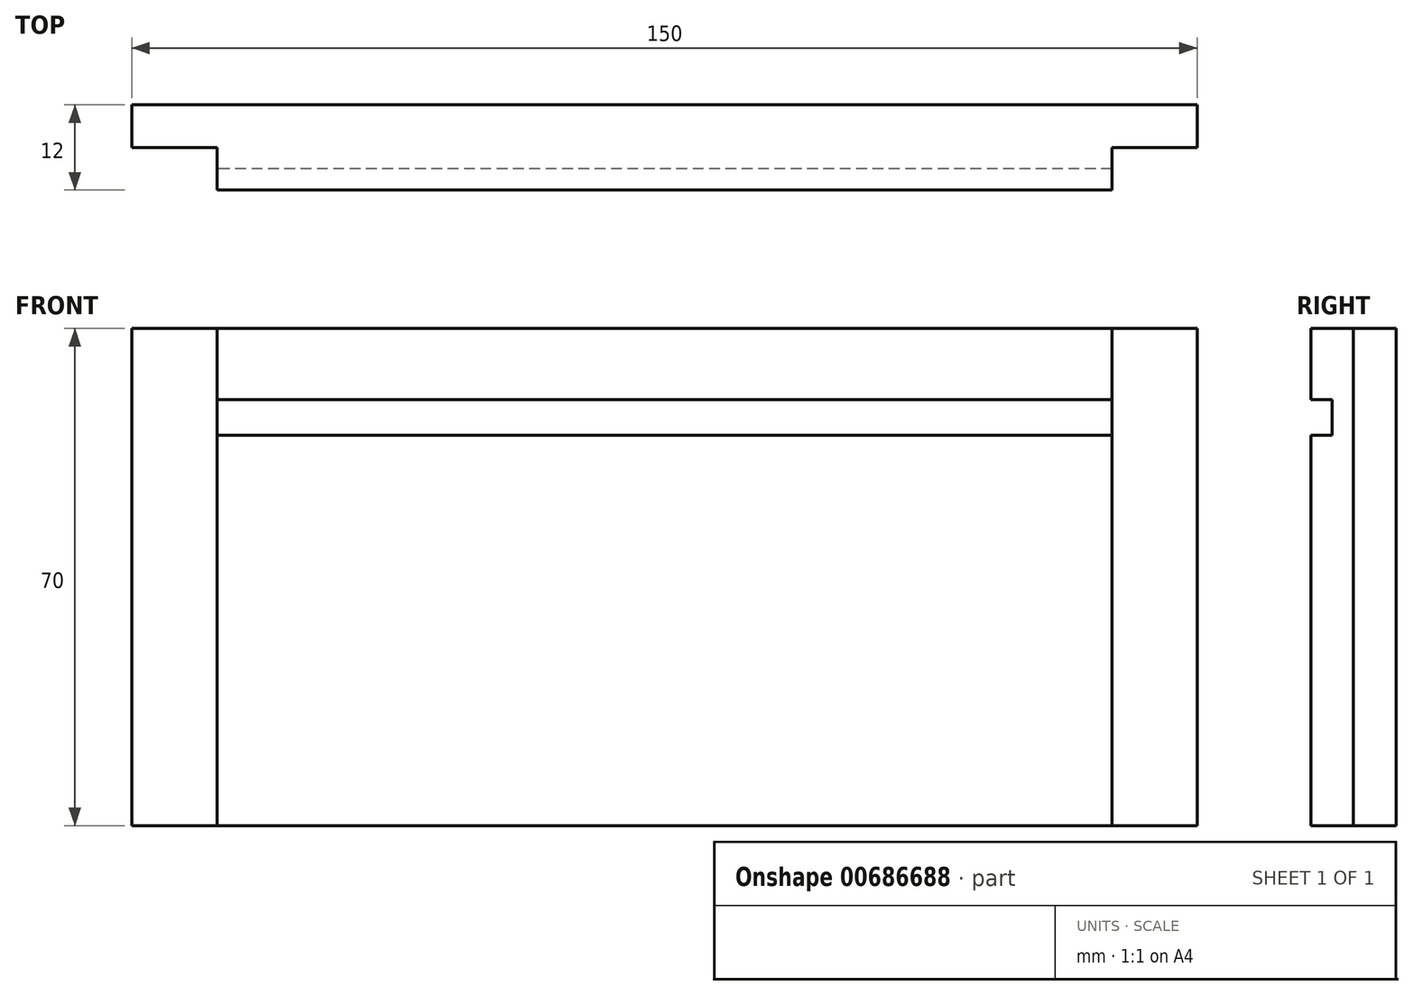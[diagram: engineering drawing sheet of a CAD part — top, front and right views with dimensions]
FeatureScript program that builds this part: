
annotation { "Feature Type Name" : "Feature", "Feature Type Description" : "" }
export const myFeature = defineFeature(function(context is Context, id is Id, definition is map)
    precondition{}
    {
        {
            var Q0;
            Q0=qCreatedBy(makeId("Right.planeOp"),FACE);
            var sketch = newSketch(context, id + "F0", { "sketchPlane" : qUnion([Q0])});
            skLineSegment(sketch, "E0", {"start": v(0, 0) * mm, "end": v(0, 70) * mm});
            skLineSegment(sketch, "E1", {"start": v(0, 70) * mm, "end": v(-12, 70) * mm});
            skLineSegment(sketch, "E2", {"start": v(-12, 70) * mm, "end": v(-12, 60) * mm});
            skLineSegment(sketch, "E3", {"start": v(-9, 60) * mm, "end": v(-12, 60) * mm});
            skLineSegment(sketch, "E4", {"start": v(-9, 60) * mm, "end": v(-9, 55) * mm});
            skLineSegment(sketch, "E5", {"start": v(-9, 55) * mm, "end": v(-12, 55) * mm});
            skLineSegment(sketch, "E6", {"start": v(-12, 55) * mm, "end": v(-12, 0) * mm});
            skLineSegment(sketch, "E7", {"start": v(-12, 0) * mm, "end": v(0, 0) * mm});
            skSolve(sketch);
        }
        {
            var Q0;
            Q0=qSketchRegion(id+"F0",true);
            var Q1;
            Q1 = qSketchRegion(id + "F2", true);
            extrude(context, id + "F1", {"entities" : qUnion([Q0, Q1]), "depth" : 150 * mm, "offsetDistance" : 25 * mm});
        }
        {
            var Q0;
            Q0=makeQuery(id+"F1.opExtrude","SWEPT_FACE",FACE,{"disambiguationData":[OSD([sQuery(id+"F0.wireOp",EDGE,"E6")])]});
            var sketch = newSketch(context, id + "F2", { "sketchPlane" : qUnion([Q0])});
            skLineSegment(sketch, "E8.bottom", {"start": v(150, 0) * mm, "end": v(138, 0) * mm});
            skLineSegment(sketch, "E8.top", {"start": v(150, 70) * mm, "end": v(138, 70) * mm});
            skLineSegment(sketch, "E8.left", {"start": v(150, 0) * mm, "end": v(150, 70) * mm});
            skLineSegment(sketch, "E8.right", {"start": v(138, 0) * mm, "end": v(138, 70) * mm});
            skLineSegment(sketch, "E9.bottom", {"start": v(0, 0) * mm, "end": v(12, 0) * mm});
            skLineSegment(sketch, "E9.top", {"start": v(0, 70) * mm, "end": v(12, 70) * mm});
            skLineSegment(sketch, "E9.left", {"start": v(0, 0) * mm, "end": v(0, 70) * mm});
            skLineSegment(sketch, "E9.right", {"start": v(12, 0) * mm, "end": v(12, 70) * mm});
            skSolve(sketch);
        }
        {
            var Q0;
            Q0=qSketchRegion(id+"F2",true);
            extrude(context, id + "F3", {"entities" : qUnion([Q0]), "operationType" : NewBodyOperationType.REMOVE, "oppositeDirection" : true, "depth" : 6 * mm, "offsetDistance" : 25 * mm});
        }
    });
